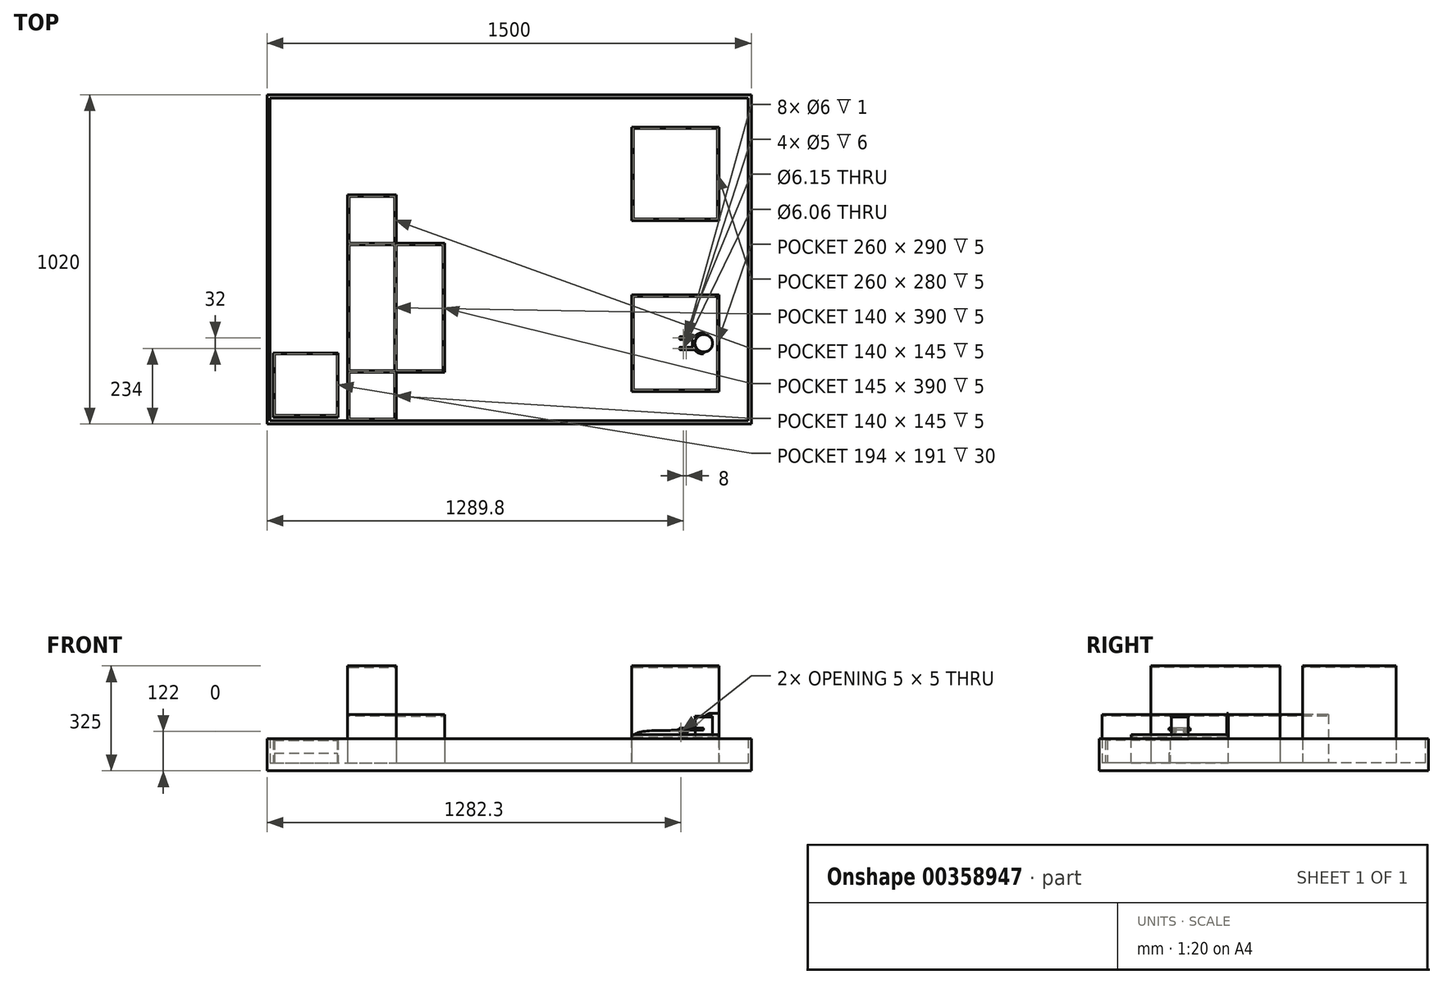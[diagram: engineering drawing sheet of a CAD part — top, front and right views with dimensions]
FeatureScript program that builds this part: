
annotation { "Feature Type Name" : "Feature", "Feature Type Description" : "" }
export const myFeature = defineFeature(function(context is Context, id is Id, definition is map)
    precondition{}
    {
        {
            var Q0;
            Q0=qCreatedBy(makeId("Top.planeOp"),FACE);
            var sketch = newSketch(context, id + "F0", { "sketchPlane" : qUnion([Q0])});
            skCircle(sketch, "E0", {"center": v(0, 0) * mm, "radius": 27.2 * mm});
            skSolve(sketch);
        }
        {
            var Q0;
            Q0=qSketchRegion(id+"F0",true);
            extrude(context, id + "F1", {"entities" : qUnion([Q0]), "depth" : 2.83 * mm});
        }
        {
            var Q0;
            Q0=makeQuery(id+"F1.opExtrude","CAP_FACE",FACE,{"disambiguationData":[OSD([sQuery(id+"F0.wireOp",EDGE,"E0")])],"isStart":false});
            var sketch = newSketch(context, id + "F2", { "sketchPlane" : qUnion([Q0])});
            skCircle(sketch, "E1", {"center": v(0, 0) * mm, "radius": 26.4 * mm});
            skSolve(sketch);
        }
        {
            var Q0;
            Q0=qSketchRegion(id+"F2",true);
            extrude(context, id + "F3", {"entities" : qUnion([Q0]), "operationType" : NewBodyOperationType.ADD, "depth" : 67.36 * mm});
        }
        {
            var Q0;
            Q0=makeQuery(id+"F3.opExtrude","CAP_FACE",FACE,{"disambiguationData":[OSD([sQuery(id+"F2.wireOp",EDGE,"E1")])],"isStart":false});
            var sketch = newSketch(context, id + "F4", { "sketchPlane" : qUnion([Q0])});
            skCircle(sketch, "E2", {"center": v(0, 0) * mm, "radius": 27.2 * mm});
            skSolve(sketch);
        }
        {
            var Q0;
            Q0=qSketchRegion(id+"F4",true);
            extrude(context, id + "F5", {"entities" : qUnion([Q0]), "operationType" : NewBodyOperationType.ADD, "depth" : 2.83 * mm});
        }
        {
            var Q0;
            Q0=makeQuery(id+"F5.opExtrude","CAP_FACE",FACE,{"disambiguationData":[OSD([sQuery(id+"F4.wireOp",EDGE,"E2")])],"isStart":false});
            var sketch = newSketch(context, id + "F6", { "sketchPlane" : qUnion([Q0])});
            skSolve(sketch);
        }
        {
            var Q0;
            Q0=qCreatedBy(makeId("Top.planeOp"),FACE);
            cPlane(context, id + "F7", {"entities" : qUnion([Q0]), "cplaneType" : CPlaneType.OFFSET, "offset" : 25 * mm, "width" : 150 * mm, "height" : 150 * mm});
        }
        {
            var Q0;
            Q0=makeQuery(id+"F6.imprint","IMPRINT",FACE,{"disambiguationData":[TD([[makeQuery(id+"F6.imprint","IMPRINT",EDGE,{"derivedFrom":makeQuery(id+"F5.opExtrude","CAP_EDGE",EDGE,{"disambiguationData":[OSD([sQuery(id+"F4.wireOp",EDGE,"E2")])],"isStart":false})}),1.0]])]});
            var sketch = newSketch(context, id + "F8", { "sketchPlane" : qUnion([Q0])});
            skSolve(sketch);
        }
        {
            var Q0;
            Q0=qCreatedBy(makeId("Top.planeOp"),FACE);
            var sketch = newSketch(context, id + "F9", { "sketchPlane" : qUnion([Q0])});
            skLineSegment(sketch, "E3.bottom", {"start": v(-222.8, -150) * mm, "end": v(47.2, -150) * mm});
            skLineSegment(sketch, "E3.top", {"start": v(-222.8, 150) * mm, "end": v(47.2, 150) * mm});
            skLineSegment(sketch, "E3.left", {"start": v(-222.8, -150) * mm, "end": v(-222.8, 150) * mm});
            skLineSegment(sketch, "E3.right", {"start": v(47.2, -150) * mm, "end": v(47.2, 150) * mm});
            skSolve(sketch);
        }
        {
            var Q0;
            Q0=qSketchRegion(id+"F9",true);
            extrude(context, id + "F10", {"entities" : qUnion([Q0]), "oppositeDirection" : true, "depth" : 72 * mm});
        }
        {
            var Q0;
            Q0=makeQuery(id+"F10.opExtrude","CAP_FACE",FACE,{"disambiguationData":[OSD([sQuery(id+"F9.wireOp",EDGE,"E3.bottom"),sQuery(id+"F9.wireOp",EDGE,"E3.top"),sQuery(id+"F9.wireOp",EDGE,"E3.left"),sQuery(id+"F9.wireOp",EDGE,"E3.right")])],"isStart":true});
            var sketch = newSketch(context, id + "F11", { "sketchPlane" : qUnion([Q0])});
            skLineSegment(sketch, "E4.bottom", {"start": v(-222.8, -150) * mm, "end": v(47.2, -150) * mm});
            skLineSegment(sketch, "E4.top", {"start": v(-222.8, -145) * mm, "end": v(42.2, -145) * mm});
            skLineSegment(sketch, "E4.left", {"start": v(-222.8, -150) * mm, "end": v(-222.8, -145) * mm});
            skLineSegment(sketch, "E5.bottom", {"start": v(47.2, 150) * mm, "end": v(42.2, 150) * mm});
            skLineSegment(sketch, "E5.left", {"start": v(47.2, 150) * mm, "end": v(47.2, -150) * mm});
            skLineSegment(sketch, "E5.right", {"start": v(42.2, 150) * mm, "end": v(42.2, -145) * mm});
            skSolve(sketch);
        }
        {
            var Q0;
            Q0=qSketchRegion(id+"F11",true);
            extrude(context, id + "F12", {"entities" : qUnion([Q0]), "operationType" : NewBodyOperationType.ADD, "depth" : 15 * mm});
        }
        {
            var Q0;
            Q0=makeQuery(id+"F12.boolean.opBoolean","MERGE",FACE,{"derivedFrom":[makeQuery(id+"F10.opExtrude","SWEPT_FACE",FACE,{"disambiguationData":[OSD([sQuery(id+"F9.wireOp",EDGE,"E3.top")])]}),makeQuery(id+"F12.opExtrude","SWEPT_FACE",FACE,{"disambiguationData":[OSD([sQuery(id+"F11.wireOp",EDGE,"E5.bottom")])]})]});
            var sketch = newSketch(context, id + "F13", { "sketchPlane" : qUnion([Q0])});
            skLineSegment(sketch, "E6", {"start": v(-47.2, 81.36) * mm, "end": v(-21.31, 81.36) * mm});
            skFitSpline(sketch, "E7", {"points": [v(-21.31, 81.36) * mm, v(15.24, 52.01) * mm, v(114.14, 28.17) * mm, v(222.8, 0) * mm], "startDerivative": vector(181.02, 0.3) * mm, "endDerivative": vector(-1.73, -239.85) * mm});
            skLineSegment(sketch, "E8", {"start": v(-47.2, 81.36) * mm, "end": v(-47.2, -72) * mm});
            skLineSegment(sketch, "E9", {"start": v(-47.2, -72) * mm, "end": v(222.8, -72) * mm});
            skLineSegment(sketch, "E10", {"start": v(222.8, -72) * mm, "end": v(222.8, 0) * mm});
            skSolve(sketch);
        }
        {
            var Q0;
            Q0=qSketchRegion(id+"F13",true);
            extrude(context, id + "F14", {"entities" : qUnion([Q0]), "operationType" : NewBodyOperationType.ADD, "oppositeDirection" : true, "depth" : 5 * mm});
        }
        {
            var Q0;
            Q0=makeQuery(id+"F10.opExtrude","CAP_FACE",FACE,{"disambiguationData":[OSD([sQuery(id+"F9.wireOp",EDGE,"E3.bottom"),sQuery(id+"F9.wireOp",EDGE,"E3.top"),sQuery(id+"F9.wireOp",EDGE,"E3.left"),sQuery(id+"F9.wireOp",EDGE,"E3.right")])],"isStart":true});
            var sketch = newSketch(context, id + "F15", { "sketchPlane" : qUnion([Q0])});
            skLineSegment(sketch, "E11.bottom", {"start": v(-222.8, 145) * mm, "end": v(-217.8, 145) * mm});
            skLineSegment(sketch, "E11.top", {"start": v(-222.8, -145) * mm, "end": v(-217.8, -145) * mm});
            skLineSegment(sketch, "E11.left", {"start": v(-222.8, 145) * mm, "end": v(-222.8, -145) * mm});
            skLineSegment(sketch, "E11.right", {"start": v(-217.8, 145) * mm, "end": v(-217.8, -145) * mm});
            skSolve(sketch);
        }
        {
            var Q0;
            Q0=qSketchRegion(id+"F15",true);
            extrude(context, id + "F16", {"entities" : qUnion([Q0]), "operationType" : NewBodyOperationType.ADD, "depth" : 5 * mm});
        }
        {
            var Q0;
            Q0=makeQuery(id+"F10.opExtrude","CAP_FACE",FACE,{"disambiguationData":[OSD([sQuery(id+"F9.wireOp",EDGE,"E3.bottom"),sQuery(id+"F9.wireOp",EDGE,"E3.top"),sQuery(id+"F9.wireOp",EDGE,"E3.left"),sQuery(id+"F9.wireOp",EDGE,"E3.right")])],"isStart":false});
            var sketch = newSketch(context, id + "F17", { "sketchPlane" : qUnion([Q0])});
            skLineSegment(sketch, "E12.bottom", {"start": v(147.2, 250) * mm, "end": v(-1352.8, 250) * mm});
            skLineSegment(sketch, "E12.top", {"start": v(147.2, -770) * mm, "end": v(-1352.8, -770) * mm});
            skLineSegment(sketch, "E12.left", {"start": v(147.2, 250) * mm, "end": v(147.2, -770) * mm});
            skLineSegment(sketch, "E12.right", {"start": v(-1352.8, 250) * mm, "end": v(-1352.8, -770) * mm});
            skSolve(sketch);
        }
        {
            var Q0;
            Q0=qSketchRegion(id+"F17",true);
            extrude(context, id + "F18", {"entities" : qUnion([Q0]), "operationType" : NewBodyOperationType.ADD, "depth" : 25 * mm});
        }
        {
            var Q0;
            Q0=makeQuery(id+"F18.opExtrude","CAP_FACE",FACE,{"disambiguationData":[OSD([sQuery(id+"F17.wireOp",EDGE,"E12.bottom"),sQuery(id+"F17.wireOp",EDGE,"E12.top"),sQuery(id+"F17.wireOp",EDGE,"E12.left"),sQuery(id+"F17.wireOp",EDGE,"E12.right")])],"isStart":true});
            var sketch = newSketch(context, id + "F19", { "sketchPlane" : qUnion([Q0])});
            skLineSegment(sketch, "E13.bottom", {"start": v(-222.8, 670) * mm, "end": v(47.2, 670) * mm});
            skLineSegment(sketch, "E13.top", {"start": v(-222.8, 380) * mm, "end": v(47.2, 380) * mm});
            skLineSegment(sketch, "E13.left", {"start": v(-222.8, 670) * mm, "end": v(-222.8, 380) * mm});
            skLineSegment(sketch, "E13.right", {"start": v(47.2, 670) * mm, "end": v(47.2, 380) * mm});
            skSolve(sketch);
        }
        {
            var Q0;
            Q0=qSketchRegion(id+"F19",true);
            extrude(context, id + "F20", {"entities" : qUnion([Q0]), "operationType" : NewBodyOperationType.ADD, "depth" : 300 * mm});
        }
        {
            var Q0;
            Q0=makeQuery(id+"F20.opExtrude","CAP_FACE",FACE,{"disambiguationData":[OSD([sQuery(id+"F19.wireOp",EDGE,"E13.bottom"),sQuery(id+"F19.wireOp",EDGE,"E13.top"),sQuery(id+"F19.wireOp",EDGE,"E13.left"),sQuery(id+"F19.wireOp",EDGE,"E13.right")])],"isStart":false});
            var sketch = newSketch(context, id + "F21", { "sketchPlane" : qUnion([Q0])});
            skLineSegment(sketch, "E14.bottom", {"start": v(-217.8, 665) * mm, "end": v(42.2, 665) * mm});
            skLineSegment(sketch, "E14.top", {"start": v(-217.8, 385) * mm, "end": v(42.2, 385) * mm});
            skLineSegment(sketch, "E14.left", {"start": v(-217.8, 665) * mm, "end": v(-217.8, 385) * mm});
            skLineSegment(sketch, "E14.right", {"start": v(42.2, 665) * mm, "end": v(42.2, 385) * mm});
            skSolve(sketch);
        }
        {
            var Q0;
            Q0=qSketchRegion(id+"F21",true);
            extrude(context, id + "F22", {"entities" : qUnion([Q0]), "operationType" : NewBodyOperationType.REMOVE, "oppositeDirection" : true, "depth" : 5 * mm});
        }
        {
            var Q0;
            Q0=makeQuery(id+"F18.opExtrude","CAP_FACE",FACE,{"disambiguationData":[OSD([sQuery(id+"F17.wireOp",EDGE,"E12.bottom"),sQuery(id+"F17.wireOp",EDGE,"E12.top"),sQuery(id+"F17.wireOp",EDGE,"E12.left"),sQuery(id+"F17.wireOp",EDGE,"E12.right")])],"isStart":true});
            var sketch = newSketch(context, id + "F23", { "sketchPlane" : qUnion([Q0])});
            skLineSegment(sketch, "E15.bottom", {"start": v(-1352.8, 770) * mm, "end": v(147.2, 770) * mm});
            skLineSegment(sketch, "E15.top", {"start": v(-1352.8, -250) * mm, "end": v(147.2, -250) * mm});
            skLineSegment(sketch, "E15.left", {"start": v(-1352.8, 770) * mm, "end": v(-1352.8, -250) * mm});
            skLineSegment(sketch, "E15.right", {"start": v(147.2, 770) * mm, "end": v(147.2, -250) * mm});
            skLineSegment(sketch, "E16.bottom", {"start": v(-1342.8, 760) * mm, "end": v(137.2, 760) * mm});
            skLineSegment(sketch, "E16.top", {"start": v(-1342.8, -240) * mm, "end": v(137.2, -240) * mm});
            skLineSegment(sketch, "E16.left", {"start": v(-1342.8, 760) * mm, "end": v(-1342.8, -240) * mm});
            skLineSegment(sketch, "E16.right", {"start": v(137.2, 760) * mm, "end": v(137.2, -240) * mm});
            skSolve(sketch);
        }
        {
            var Q0;
            Q0=qSketchRegion(id+"F23",true);
            extrude(context, id + "F24", {"entities" : qUnion([Q0]), "operationType" : NewBodyOperationType.ADD, "depth" : 75 * mm});
        }
        {
            var Q0;
            Q0=makeQuery(id+"F18.opExtrude","CAP_FACE",FACE,{"disambiguationData":[OSD([sQuery(id+"F17.wireOp",EDGE,"E12.bottom"),sQuery(id+"F17.wireOp",EDGE,"E12.top"),sQuery(id+"F17.wireOp",EDGE,"E12.left"),sQuery(id+"F17.wireOp",EDGE,"E12.right")])],"isStart":true});
            var sketch = newSketch(context, id + "F25", { "sketchPlane" : qUnion([Q0])});
            skLineSegment(sketch, "E17.bottom", {"start": v(-1102.8, 460) * mm, "end": v(-952.8, 460) * mm});
            skLineSegment(sketch, "E17.top", {"start": v(-1102.8, -240) * mm, "end": v(-952.8, -240) * mm});
            skLineSegment(sketch, "E17.left", {"start": v(-1102.8, 460) * mm, "end": v(-1102.8, -240) * mm});
            skLineSegment(sketch, "E17.right", {"start": v(-952.8, 460) * mm, "end": v(-952.8, 310) * mm});
            skLineSegment(sketch, "E18.bottom", {"start": v(-952.8, 310) * mm, "end": v(-802.8, 310) * mm});
            skLineSegment(sketch, "E18.top", {"start": v(-952.8, -90) * mm, "end": v(-802.8, -90) * mm});
            skLineSegment(sketch, "E18.right", {"start": v(-802.8, 310) * mm, "end": v(-802.8, -90) * mm});
            skLineSegment(sketch, "E19.trimOffspring", {"start": v(-952.8, -90) * mm, "end": v(-952.8, -240) * mm});
            skSolve(sketch);
        }
        {
            var Q0;
            Q0=qSketchRegion(id+"F25",true);
            extrude(context, id + "F26", {"entities" : qUnion([Q0]), "operationType" : NewBodyOperationType.ADD, "depth" : 150 * mm});
        }
        {
            var Q0;
            Q0=makeQuery(id+"F26.opExtrude","CAP_FACE",FACE,{"disambiguationData":[OSD([sQuery(id+"F25.wireOp",EDGE,"E17.bottom"),sQuery(id+"F25.wireOp",EDGE,"E17.top"),sQuery(id+"F25.wireOp",EDGE,"E17.left"),sQuery(id+"F25.wireOp",EDGE,"E17.right"),sQuery(id+"F25.wireOp",EDGE,"E18.bottom"),sQuery(id+"F25.wireOp",EDGE,"E18.top"),sQuery(id+"F25.wireOp",EDGE,"E18.right"),sQuery(id+"F25.wireOp",EDGE,"E19.trimOffspring")])],"isStart":false});
            var sketch = newSketch(context, id + "F27", { "sketchPlane" : qUnion([Q0])});
            skLineSegment(sketch, "E20.bottom", {"start": v(-952.8, 310) * mm, "end": v(-1102.8, 310) * mm});
            skLineSegment(sketch, "E20.top", {"start": v(-952.8, -90) * mm, "end": v(-1102.8, -90) * mm});
            skLineSegment(sketch, "E20.left", {"start": v(-952.8, 310) * mm, "end": v(-952.8, -90) * mm});
            skLineSegment(sketch, "E20.right", {"start": v(-1102.8, 310) * mm, "end": v(-1102.8, -90) * mm});
            skSolve(sketch);
        }
        {
            var Q0;
            Q0=qSketchRegion(id+"F27",true);
            extrude(context, id + "F28", {"entities" : qUnion([Q0]), "operationType" : NewBodyOperationType.ADD, "depth" : 150 * mm});
        }
        {
            var Q0;
            Q0=makeQuery(id+"F28.opExtrude","CAP_FACE",FACE,{"disambiguationData":[OSD([sQuery(id+"F27.wireOp",EDGE,"E20.bottom"),sQuery(id+"F27.wireOp",EDGE,"E20.top"),sQuery(id+"F27.wireOp",EDGE,"E20.left"),sQuery(id+"F27.wireOp",EDGE,"E20.right")])],"isStart":false});
            var sketch = newSketch(context, id + "F29", { "sketchPlane" : qUnion([Q0])});
            skLineSegment(sketch, "E21.bottom", {"start": v(-1097.8, 305) * mm, "end": v(-957.8, 305) * mm});
            skLineSegment(sketch, "E21.top", {"start": v(-1097.8, -85) * mm, "end": v(-957.8, -85) * mm});
            skLineSegment(sketch, "E21.left", {"start": v(-1097.8, 305) * mm, "end": v(-1097.8, -85) * mm});
            skLineSegment(sketch, "E21.right", {"start": v(-957.8, 305) * mm, "end": v(-957.8, -85) * mm});
            skSolve(sketch);
        }
        {
            var Q0;
            Q0=qSketchRegion(id+"F29",true);
            extrude(context, id + "F30", {"entities" : qUnion([Q0]), "operationType" : NewBodyOperationType.REMOVE, "oppositeDirection" : true, "depth" : 5 * mm});
        }
        {
            var Q0;
            {var subQ0=sQuery(id+"F25.wireOp",EDGE,"E17.left");var subQ1=sQuery(id+"F25.wireOp",EDGE,"E18.bottom");var subQ2=sQuery(id+"F25.wireOp",EDGE,"E17.right");var subQ3=sQuery(id+"F25.wireOp",EDGE,"E17.bottom");var subQ4=makeQuery(id+"F26.opExtrude","CAP_FACE",FACE,{"disambiguationData":[OSD([subQ3,sQuery(id+"F25.wireOp",EDGE,"E17.top"),subQ0,subQ2,subQ1,sQuery(id+"F25.wireOp",EDGE,"E18.top"),sQuery(id+"F25.wireOp",EDGE,"E18.right"),sQuery(id+"F25.wireOp",EDGE,"E19.trimOffspring")])],"isStart":false});Q0=makeQuery(id+"F28.boolean.opBoolean","SPLIT",FACE,{"disambiguationData":[TD([makeQuery(id+"F26.opExtrude","SWEPT_FACE",FACE,{"disambiguationData":[OSD([subQ3])]})])],"derivedFrom":subQ4});}
            var sketch = newSketch(context, id + "F31", { "sketchPlane" : qUnion([Q0])});
            skLineSegment(sketch, "E22.bottom", {"start": v(-1097.8, 455) * mm, "end": v(-957.8, 455) * mm});
            skLineSegment(sketch, "E22.top", {"start": v(-1097.8, 310) * mm, "end": v(-957.8, 310) * mm});
            skLineSegment(sketch, "E22.left", {"start": v(-1097.8, 455) * mm, "end": v(-1097.8, 310) * mm});
            skLineSegment(sketch, "E22.right", {"start": v(-957.8, 455) * mm, "end": v(-957.8, 310) * mm});
            skLineSegment(sketch, "E23.bottom", {"start": v(-952.8, 305) * mm, "end": v(-807.8, 305) * mm});
            skLineSegment(sketch, "E23.top", {"start": v(-952.8, -85) * mm, "end": v(-807.8, -85) * mm});
            skLineSegment(sketch, "E23.left", {"start": v(-952.8, 305) * mm, "end": v(-952.8, -85) * mm});
            skLineSegment(sketch, "E23.right", {"start": v(-807.8, 305) * mm, "end": v(-807.8, -85) * mm});
            skLineSegment(sketch, "E24.bottom", {"start": v(-1097.8, -90) * mm, "end": v(-957.8, -90) * mm});
            skLineSegment(sketch, "E24.top", {"start": v(-1097.8, -235) * mm, "end": v(-957.8, -235) * mm});
            skLineSegment(sketch, "E24.left", {"start": v(-1097.8, -90) * mm, "end": v(-1097.8, -235) * mm});
            skLineSegment(sketch, "E24.right", {"start": v(-957.8, -90) * mm, "end": v(-957.8, -235) * mm});
            skSolve(sketch);
        }
        {
            var Q0;
            Q0=qSketchRegion(id+"F31",true);
            extrude(context, id + "F32", {"entities" : qUnion([Q0]), "operationType" : NewBodyOperationType.REMOVE, "oppositeDirection" : true, "depth" : 5 * mm});
        }
        {
            var Q0;
            Q0=qCreatedBy(id+"F7.planeOp",FACE);
            var sketch = newSketch(context, id + "F33", { "sketchPlane" : qUnion([Q0])});
            skLineSegment(sketch, "E25", {"start": v(0, 0) * mm, "end": v(-90, 0) * mm, "construction": true});
            skLineSegment(sketch, "E26.bottom", {"start": v(-74.5, -12) * mm, "end": v(-55, -12) * mm});
            skLineSegment(sketch, "E26.top", {"start": v(-74.5, -20) * mm, "end": v(-55, -20) * mm});
            skLineSegment(sketch, "E26.left", {"start": v(-74.5, -12) * mm, "end": v(-74.5, -13) * mm});
            skPoint(sketch, "E27.visualSharp", {"position": v(-51, -12) * mm});
            skPoint(sketch, "E28.visualSharp", {"position": v(-51, -20) * mm});
            skCircle(sketch, "E29", {"center": v(-55, -16) * mm, "radius": 3 * mm});
            skLineSegment(sketch, "E30", {"start": v(-59, -3.98) * mm, "end": v(-59, -18.08) * mm, "construction": true});
            skCircle(sketch, "E31.MirrorC", {"center": v(-63, -16) * mm, "radius": 3 * mm});
            skLineSegment(sketch, "E32.bottom", {"start": v(-74.5, -13) * mm, "end": v(-65.65, -13) * mm});
            skLineSegment(sketch, "E32.top", {"start": v(-74.5, -19) * mm, "end": v(-65.65, -19) * mm});
            skArc(sketch, "E33", {"start": v(-65.65, -13) * mm, "mid": v(-67, -16) * mm, "end": v(-65.65, -19) * mm});
            skLineSegment(sketch, "E34.trimOffspring", {"start": v(-74.5, -19) * mm, "end": v(-74.5, -20) * mm});
            skArc(sketch, "E35.trimOffspring", {"start": v(-55, -20) * mm, "mid": v(-51, -16) * mm, "end": v(-55, -12) * mm});
            skLineSegment(sketch, "E36.MirrorCS", {"start": v(-74.5, 12) * mm, "end": v(-74.5, 13) * mm});
            skLineSegment(sketch, "E37.MirrorCS", {"start": v(-74.5, 19) * mm, "end": v(-74.5, 20) * mm});
            skPoint(sketch, "E38.MirrorP", {"position": v(-51, 12) * mm});
            skLineSegment(sketch, "E39.MirrorCS", {"start": v(-74.5, 12) * mm, "end": v(-55, 12) * mm});
            skPoint(sketch, "E40.MirrorP", {"position": v(-51, 20) * mm});
            skArc(sketch, "E41.MirrorCS", {"start": v(-65.65, 13) * mm, "mid": v(-67, 16) * mm, "end": v(-65.65, 19) * mm});
            skArc(sketch, "E42.MirrorCS", {"start": v(-55, 20) * mm, "mid": v(-51, 16) * mm, "end": v(-55, 12) * mm});
            skLineSegment(sketch, "E43.MirrorCS", {"start": v(-74.5, 20) * mm, "end": v(-55, 20) * mm});
            skCircle(sketch, "E44.MirrorC", {"center": v(-55, 16) * mm, "radius": 3 * mm});
            skCircle(sketch, "E45.MirrorC", {"center": v(-63, 16) * mm, "radius": 3 * mm});
            skLineSegment(sketch, "E46.MirrorCS", {"start": v(-74.5, 19) * mm, "end": v(-65.65, 19) * mm});
            skLineSegment(sketch, "E47.MirrorCS", {"start": v(-74.5, 13) * mm, "end": v(-65.65, 13) * mm});
            skSolve(sketch);
        }
        {
            var Q0;
            Q0=qSketchRegion(id+"F33",true);
            var Q1;
            Q1=qSketchRegion(id+"F36",true);
            extrude(context, id + "F34", {"entities" : qUnion([Q0, Q1]), "endBound" : BoundingType.SYMMETRIC, "depth" : 8 * mm});
        }
        {
            var Q0;
            Q0=makeQuery(id+"F34.opExtrude","CAP_EDGE",EDGE,{"disambiguationData":[OSD([sQuery(id+"F33.wireOp",EDGE,"E34.trimOffspring")])],"isStart":false});
            var Q1;
            Q1=makeQuery(id+"F34.opExtrude","CAP_EDGE",EDGE,{"disambiguationData":[OSD([sQuery(id+"F33.wireOp",EDGE,"E26.left")])],"isStart":false});
            var Q2;
            Q2=makeQuery(id+"F34.opExtrude","CAP_EDGE",EDGE,{"disambiguationData":[OSD([sQuery(id+"F33.wireOp",EDGE,"E34.trimOffspring")])],"isStart":true});
            var Q3;
            Q3=makeQuery(id+"F34.opExtrude","CAP_EDGE",EDGE,{"disambiguationData":[OSD([sQuery(id+"F33.wireOp",EDGE,"E26.left")])],"isStart":true});
            var Q4;
            Q4=makeQuery(id+"F34.opExtrude","CAP_EDGE",EDGE,{"disambiguationData":[OSD([sQuery(id+"F33.wireOp",EDGE,"E36.MirrorCS")])],"isStart":false});
            var Q5;
            Q5=makeQuery(id+"F34.opExtrude","CAP_EDGE",EDGE,{"disambiguationData":[OSD([sQuery(id+"F33.wireOp",EDGE,"E37.MirrorCS")])],"isStart":false});
            var Q6;
            Q6=makeQuery(id+"F34.opExtrude","CAP_EDGE",EDGE,{"disambiguationData":[OSD([sQuery(id+"F33.wireOp",EDGE,"E37.MirrorCS")])],"isStart":true});
            var Q7;
            Q7=makeQuery(id+"F34.opExtrude","CAP_EDGE",EDGE,{"disambiguationData":[OSD([sQuery(id+"F33.wireOp",EDGE,"E36.MirrorCS")])],"isStart":true});
            fillet(context, id + "F35", {"entities" : qUnion([Q0, Q1, Q2, Q3, Q4, Q5, Q6, Q7]), "radius" : 4 * mm, "tangentPropagation" : true, "allowEdgeOverflow" : false});
        }
        {
            var Q0;
            Q0=makeQuery(id+"F34.opExtrude","SWEPT_FACE",FACE,{"disambiguationData":[OSD([sQuery(id+"F33.wireOp",EDGE,"E26.top")])]});
            var sketch = newSketch(context, id + "F36", { "sketchPlane" : qUnion([Q0])});
            skCircle(sketch, "E48", {"center": v(-70.5, 25) * mm, "radius": 3 * mm});
            skSolve(sketch);
        }
        {
            var Q0;
            Q0=qSketchRegion(id+"F36",true);
            var Q1;
            Q1=makeQuery(id+"F34.opExtrude","SWEPT_FACE",FACE,{"disambiguationData":[OSD([sQuery(id+"F33.wireOp",EDGE,"E26.bottom")])]});
            extrude(context, id + "F37", {"entities" : qUnion([Q0]), "operationType" : NewBodyOperationType.ADD, "endBound" : BoundingType.UP_TO_SURFACE, "oppositeDirection" : true, "endBoundEntityFace" : qUnion([Q1]), "depth" : 25 * mm});
        }
        {
            var Q0;
            Q0=makeQuery(id+"F34.opExtrude","SWEPT_FACE",FACE,{"disambiguationData":[OSD([sQuery(id+"F33.wireOp",EDGE,"E43.MirrorCS")])]});
            var sketch = newSketch(context, id + "F38", { "sketchPlane" : qUnion([Q0])});
            skCircle(sketch, "E49", {"center": v(70.5, 25) * mm, "radius": 3 * mm});
            skSolve(sketch);
        }
        {
            var Q0;
            Q0=qSketchRegion(id+"F38",true);
            var Q1;
            Q1=makeQuery(id+"F34.opExtrude","SWEPT_FACE",FACE,{"disambiguationData":[OSD([sQuery(id+"F33.wireOp",EDGE,"E39.MirrorCS")])]});
            extrude(context, id + "F39", {"entities" : qUnion([Q0]), "operationType" : NewBodyOperationType.ADD, "endBound" : BoundingType.UP_TO_SURFACE, "oppositeDirection" : true, "endBoundEntityFace" : qUnion([Q1]), "depth" : 25 * mm});
        }
        {
            var Q0;
            Q0=qCreatedBy(id+"F7.planeOp",FACE);
            var sketch = newSketch(context, id + "F40", { "sketchPlane" : qUnion([Q0])});
            skCircle(sketch, "E50", {"center": v(-55, 16) * mm, "radius": 3 * mm});
            skCircle(sketch, "E51", {"center": v(-63, 16) * mm, "radius": 2.5 * mm});
            skCircle(sketch, "E52", {"center": v(-63, 16) * mm, "radius": 3 * mm});
            skCircle(sketch, "E53", {"center": v(-55, 16) * mm, "radius": 2.5 * mm});
            skSolve(sketch);
        }
        {
            var Q0;
            Q0=qSketchRegion(id+"F40",true);
            extrude(context, id + "F41", {"entities" : qUnion([Q0]), "operationType" : NewBodyOperationType.ADD, "endBound" : BoundingType.SYMMETRIC, "depth" : 6 * mm});
        }
        {
            var Q0;
            Q0=qCreatedBy(id+"F7.planeOp",FACE);
            var sketch = newSketch(context, id + "F42", { "sketchPlane" : qUnion([Q0])});
            skCircle(sketch, "E54", {"center": v(-63, -16) * mm, "radius": 2.5 * mm});
            skCircle(sketch, "E55", {"center": v(-63, -16) * mm, "radius": 3 * mm});
            skCircle(sketch, "E56", {"center": v(-55, -16) * mm, "radius": 2.5 * mm});
            skCircle(sketch, "E57", {"center": v(-55, -16) * mm, "radius": 3 * mm});
            skSolve(sketch);
        }
        {
            var Q0;
            Q0=qSketchRegion(id+"F42",true);
            extrude(context, id + "F43", {"entities" : qUnion([Q0]), "operationType" : NewBodyOperationType.ADD, "endBound" : BoundingType.SYMMETRIC, "depth" : 6 * mm});
        }
        {
            var Q0;
            Q0=makeQuery(id+"F34.opExtrude","SWEPT_FACE",FACE,{"disambiguationData":[OSD([sQuery(id+"F33.wireOp",EDGE,"E43.MirrorCS")])]});
            var sketch = newSketch(context, id + "F44", { "sketchPlane" : qUnion([Q0])});
            skArc(sketch, "E58", {"start": v(71.5, 27.3) * mm, "mid": v(70.5, 27.5) * mm, "end": v(69.5, 27.3) * mm});
            skLineSegment(sketch, "E59.bottom", {"start": v(68.2, 26) * mm, "end": v(69.5, 26) * mm});
            skLineSegment(sketch, "E59.top", {"start": v(68.2, 24) * mm, "end": v(69.5, 24) * mm});
            skLineSegment(sketch, "E60.left", {"start": v(71.5, 27.3) * mm, "end": v(71.5, 26) * mm});
            skLineSegment(sketch, "E60.right", {"start": v(69.5, 27.3) * mm, "end": v(69.5, 26) * mm});
            skPoint(sketch, "E61.orphan", {"position": v(69.5, 27.8) * mm});
            skPoint(sketch, "E62.orphan", {"position": v(71.5, 27.8) * mm});
            skArc(sketch, "E63.trimOffspring", {"start": v(68.2, 26) * mm, "mid": v(68, 25) * mm, "end": v(68.2, 24) * mm});
            skPoint(sketch, "E59.left.start.orphan", {"position": v(67.32, 26) * mm});
            skPoint(sketch, "E64.orphan", {"position": v(67.32, 24) * mm});
            skArc(sketch, "E65.trimOffspring", {"start": v(69.5, 22.7) * mm, "mid": v(70.5, 22.5) * mm, "end": v(71.5, 22.7) * mm});
            skLineSegment(sketch, "E66.trimOffspring", {"start": v(69.5, 24) * mm, "end": v(69.5, 22.7) * mm});
            skLineSegment(sketch, "E67.trimOffspring", {"start": v(71.5, 26) * mm, "end": v(72.8, 26) * mm});
            skLineSegment(sketch, "E68.trimOffspring", {"start": v(71.5, 24) * mm, "end": v(71.5, 22.7) * mm});
            skLineSegment(sketch, "E69.trimOffspring", {"start": v(71.5, 24) * mm, "end": v(72.8, 24) * mm});
            skPoint(sketch, "E60.top.end.orphan", {"position": v(69.5, 22.2) * mm});
            skPoint(sketch, "E70.orphan", {"position": v(71.5, 22.2) * mm});
            skPoint(sketch, "E59.right.end.orphan", {"position": v(73.68, 24) * mm});
            skPoint(sketch, "E71.orphan", {"position": v(73.68, 26) * mm});
            skArc(sketch, "E72.trimOffspring", {"start": v(72.8, 24) * mm, "mid": v(73, 25) * mm, "end": v(72.8, 26) * mm});
            skSolve(sketch);
        }
        {
            var Q0;
            Q0=qSketchRegion(id+"F44",true);
            extrude(context, id + "F45", {"entities" : qUnion([Q0]), "operationType" : NewBodyOperationType.REMOVE, "endBound" : BoundingType.THROUGH_ALL, "oppositeDirection" : true, "depth" : 25 * mm});
        }
        {
            var Q0;
            Q0=makeQuery(id+"F18.opExtrude","CAP_FACE",FACE,{"disambiguationData":[OSD([sQuery(id+"F17.wireOp",EDGE,"E12.bottom"),sQuery(id+"F17.wireOp",EDGE,"E12.top"),sQuery(id+"F17.wireOp",EDGE,"E12.left"),sQuery(id+"F17.wireOp",EDGE,"E12.right")])],"isStart":true});
            var sketch = newSketch(context, id + "F46", { "sketchPlane" : qUnion([Q0])});
            skLineSegment(sketch, "E73.bottom", {"start": v(-1332.8, -30) * mm, "end": v(-1132.8, -30) * mm});
            skLineSegment(sketch, "E73.top", {"start": v(-1332.8, -230) * mm, "end": v(-1132.8, -230) * mm});
            skLineSegment(sketch, "E73.left", {"start": v(-1332.8, -30) * mm, "end": v(-1332.8, -230) * mm});
            skLineSegment(sketch, "E73.right", {"start": v(-1132.8, -30) * mm, "end": v(-1132.8, -230) * mm});
            skLineSegment(sketch, "E74.bottom", {"start": v(-1329.8, -33) * mm, "end": v(-1135.8, -33) * mm});
            skLineSegment(sketch, "E74.top", {"start": v(-1329.8, -224) * mm, "end": v(-1135.8, -224) * mm});
            skLineSegment(sketch, "E74.left", {"start": v(-1329.8, -33) * mm, "end": v(-1329.8, -224) * mm});
            skLineSegment(sketch, "E74.right", {"start": v(-1135.8, -33) * mm, "end": v(-1135.8, -224) * mm});
            skSolve(sketch);
        }
        {
            var Q0;
            Q0=qSketchRegion(id+"F46",true);
            extrude(context, id + "F47", {"entities" : qUnion([Q0]), "operationType" : NewBodyOperationType.ADD, "depth" : 30 * mm});
        }
        {
            var Q0;
            Q0=makeQuery(id+"F47.opExtrude","CAP_FACE",FACE,{"disambiguationData":[OSD([sQuery(id+"F46.wireOp",EDGE,"E73.bottom"),sQuery(id+"F46.wireOp",EDGE,"E73.top"),sQuery(id+"F46.wireOp",EDGE,"E73.left"),sQuery(id+"F46.wireOp",EDGE,"E73.right"),sQuery(id+"F46.wireOp",EDGE,"E74.bottom"),sQuery(id+"F46.wireOp",EDGE,"E74.top"),sQuery(id+"F46.wireOp",EDGE,"E74.left"),sQuery(id+"F46.wireOp",EDGE,"E74.right")])],"isStart":false});
            var sketch = newSketch(context, id + "F48", { "sketchPlane" : qUnion([Q0])});
            skLineSegment(sketch, "E75.bottom", {"start": v(-1332.8, -30) * mm, "end": v(-1329.8, -30) * mm});
            skLineSegment(sketch, "E75.top", {"start": v(-1332.8, -230) * mm, "end": v(-1329.8, -230) * mm});
            skLineSegment(sketch, "E75.left", {"start": v(-1332.8, -30) * mm, "end": v(-1332.8, -230) * mm});
            skLineSegment(sketch, "E75.right", {"start": v(-1329.8, -30) * mm, "end": v(-1329.8, -224) * mm});
            skLineSegment(sketch, "E76.bottom", {"start": v(-1329.8, -230) * mm, "end": v(-1135.8, -230) * mm});
            skLineSegment(sketch, "E76.top", {"start": v(-1329.8, -224) * mm, "end": v(-1135.8, -224) * mm});
            skLineSegment(sketch, "E77.bottom", {"start": v(-1135.8, -230) * mm, "end": v(-1132.8, -230) * mm});
            skLineSegment(sketch, "E77.top", {"start": v(-1135.8, -30) * mm, "end": v(-1132.8, -30) * mm});
            skLineSegment(sketch, "E77.left", {"start": v(-1135.8, -224) * mm, "end": v(-1135.8, -30) * mm});
            skLineSegment(sketch, "E77.right", {"start": v(-1132.8, -230) * mm, "end": v(-1132.8, -30) * mm});
            skSolve(sketch);
        }
        {
            var Q0;
            Q0=qSketchRegion(id+"F48",true);
            extrude(context, id + "F49", {"entities" : qUnion([Q0]), "operationType" : NewBodyOperationType.ADD, "depth" : 40 * mm});
        }
        {
            var Q0;
            Q0=makeQuery(id+"F34.opExtrude","CAP_FACE",FACE,{"disambiguationData":[OSD([sQuery(id+"F33.wireOp",EDGE,"E26.bottom"),sQuery(id+"F33.wireOp",EDGE,"E26.top"),sQuery(id+"F33.wireOp",EDGE,"E26.left"),sQuery(id+"F33.wireOp",EDGE,"E29"),sQuery(id+"F33.wireOp",EDGE,"E31.MirrorC"),sQuery(id+"F33.wireOp",EDGE,"E32.bottom"),sQuery(id+"F33.wireOp",EDGE,"E32.top"),sQuery(id+"F33.wireOp",EDGE,"E33"),sQuery(id+"F33.wireOp",EDGE,"E34.trimOffspring"),sQuery(id+"F33.wireOp",EDGE,"E35.trimOffspring")])],"isStart":false});
            var sketch = newSketch(context, id + "F50", { "sketchPlane" : qUnion([Q0])});
            skLineSegment(sketch, "E78", {"start": v(-75, 17) * mm, "end": v(-75, 14.93) * mm});
            skLineSegment(sketch, "E79", {"start": v(-74.5, -15) * mm, "end": v(-74.5, -17) * mm});
            skLineSegment(sketch, "E80", {"start": v(-71.5, -20) * mm, "end": v(-28.91, -20) * mm});
            skArc(sketch, "E81", {"start": v(-0.37, 27.9) * mm, "mid": v(-28, 0.1) * mm, "end": v(-0.83, -28.16) * mm});
            skLineSegment(sketch, "E82", {"start": v(-0.37, 27.9) * mm, "end": v(-0.37, 32.92) * mm});
            skLineSegment(sketch, "E83", {"start": v(-0.83, -28.16) * mm, "end": v(-0.83, -33.18) * mm});
            skArc(sketch, "E84", {"start": v(-0.37, 32.92) * mm, "mid": v(-16.17, 30) * mm, "end": v(-28.73, 20) * mm});
            skLineSegment(sketch, "E85", {"start": v(-72, 11.93) * mm, "end": v(-33.28, 11.93) * mm});
            skLineSegment(sketch, "E86", {"start": v(-72, 20) * mm, "end": v(-28.73, 20) * mm});
            skLineSegment(sketch, "E87", {"start": v(-71.5, -12) * mm, "end": v(-33.28, -12) * mm});
            skCircle(sketch, "E88", {"center": v(-63, 16) * mm, "radius": 3.08 * mm});
            skCircle(sketch, "E89", {"center": v(-55, 16) * mm, "radius": 3 * mm});
            skCircle(sketch, "E90", {"center": v(-63, -16) * mm, "radius": 3.03 * mm});
            skCircle(sketch, "E91", {"center": v(-55, -16) * mm, "radius": 2.99 * mm});
            skArc(sketch, "E92.trimOffspring", {"start": v(-33.28, 11.93) * mm, "mid": v(-35.55, -0.03) * mm, "end": v(-33.34, -12) * mm});
            skArc(sketch, "E93.trimOffspring", {"start": v(-28.91, -20) * mm, "mid": v(-16.51, -30.08) * mm, "end": v(-0.83, -33.18) * mm});
            skArc(sketch, "E94.filletArc", {"start": v(-72, 20) * mm, "mid": v(-74.12, 19.12) * mm, "end": v(-75, 17) * mm});
            skArc(sketch, "E95.filletArc", {"start": v(-75, 14.93) * mm, "mid": v(-74.12, 12.81) * mm, "end": v(-72, 11.93) * mm});
            skArc(sketch, "E96.filletArc", {"start": v(-71.5, -12) * mm, "mid": v(-73.63, -12.88) * mm, "end": v(-74.5, -15) * mm});
            skArc(sketch, "E97.filletArc", {"start": v(-74.5, -17) * mm, "mid": v(-73.63, -19.13) * mm, "end": v(-71.5, -20) * mm});
            skSolve(sketch);
        }
        {
            var Q0;
            Q0 = qSketchRegion(id + "F50", true);
            var Q1;
            Q1=makeQuery(id+"F10.opExtrude","CAP_FACE",FACE,{"disambiguationData":[OSD([sQuery(id+"F9.wireOp",EDGE,"E3.bottom"),sQuery(id+"F9.wireOp",EDGE,"E3.top"),sQuery(id+"F9.wireOp",EDGE,"E3.left"),sQuery(id+"F9.wireOp",EDGE,"E3.right")])],"isStart":true});
            extrude(context, id + "F51", {"entities" : qUnion([Q0, Q1]), "depth" : 6 * mm});
        }
    });
